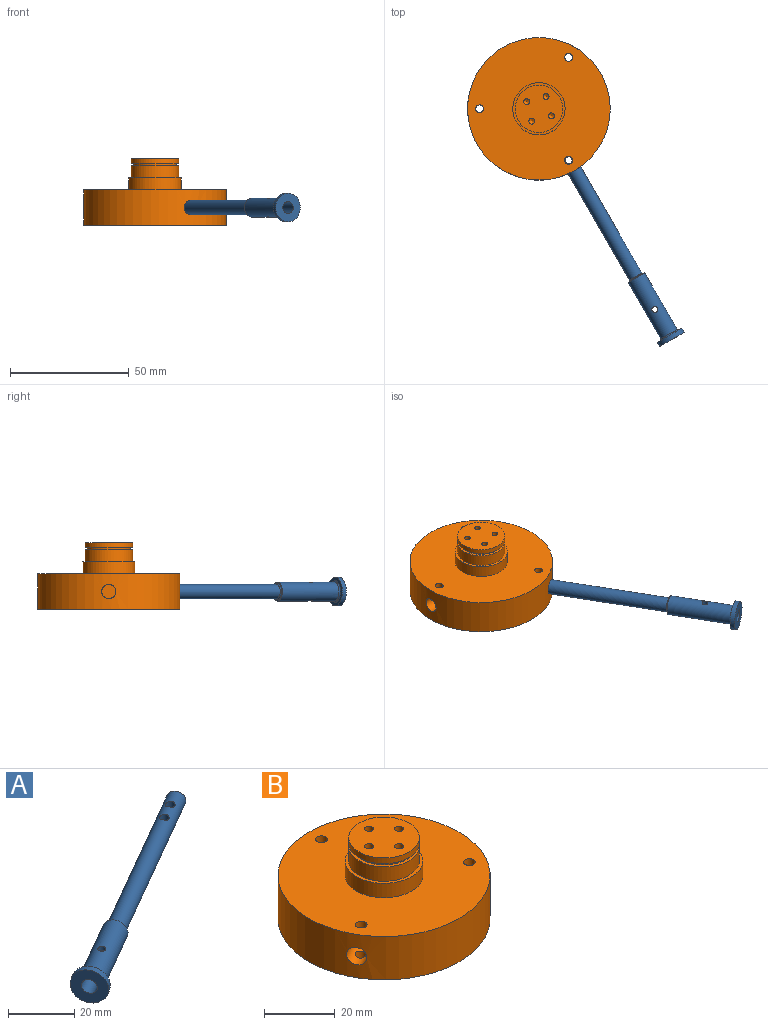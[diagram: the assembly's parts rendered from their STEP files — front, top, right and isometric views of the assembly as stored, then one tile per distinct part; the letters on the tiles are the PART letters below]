
ASSEMBLY  parts=2 mates=1
PART A: 16 faces, bbox 92.3x58.3x12 mm
  f0: cylinder r=6mm len=12mm, axis (0.87,0.5,0), area 75.4mm2, adj f1,f2
  f1: plane 12x10.39mm, normal (-0.87,-0.5,0), area 93.5mm2, adj f0,f10
  f2: plane 12x10.39mm, normal (0.87,0.5,0), area 49.5mm2, adj f0,f8
  f3: cylinder r=4mm len=27.82mm, axis (-0.87,-0.5,0), area 681.2mm2, adj f4,f8,f11,f12
  f4: plane 8x6.93mm, normal (0.87,0.5,0), area 11.8mm2, adj f3,f7
  f5: plane 4x3.46mm, normal (0.87,0.5,0), area 12.6mm2, adj f15
  f6: cylinder r=3mm len=64.05mm, axis (0.87,0.5,0), area 1299.6mm2, adj f7,f13,f14,f15
  f7: torus R=3.5mm, axis (0.87,0.5,0), area 15.7mm2, adj f4,f6
  f8: torus R=4.5mm, axis (-0.87,-0.5,0), area 20.6mm2, adj f2,f3
  f9: cone r=0mm half-angle=59deg, axis (-0.87,-0.5,0), area 22.9mm2, adj f10
  f10: cylinder r=2.5mm len=24.15mm, axis (-0.87,-0.5,0), area 382.5mm2, adj f1,f9,f11,f12
  f11: cylinder r=1.25mm len=2.5mm, axis (0,0,1), area 12.3mm2, adj f3,f10
  f12: cylinder r=1.25mm len=2.5mm, axis (0,0,1), area 12.3mm2, adj f3,f10
  f13: cylinder r=1.5mm len=6mm, axis (0,0,1), area 52.8mm2, adj f6
  f14: cylinder r=1.5mm len=6mm, axis (0,0,1), area 52.8mm2, adj f6
  f15: cone r=2mm half-angle=45deg, axis (-0.87,-0.5,0), area 22.2mm2, adj f5,f6
PART B: 33 faces, bbox 60x60x28.1 mm
  f0: cylinder r=3mm len=20.32mm, axis (0.87,0.5,0), area 357.7mm2, adj f3,f12,f13,f14
  f1: cylinder r=3mm len=20.32mm, axis (-0.87,0.5,0), area 357.7mm2, adj f3,f9,f10,f11
  f2: cylinder r=3mm len=20mm, axis (0,-1,0), area 357.7mm2, adj f3,f6,f7,f8
  f3: cylinder r=30mm len=60mm, axis (0,0,-1), area 2742.6mm2, adj f0,f1,f2,f4,f5
  f4: plane 60x60mm, normal (0,0,1), area 2421.6mm2, adj f3,f7,f10,f13,f15
  f5: plane 60x60mm, normal (0,0,-1), area 2793.2mm2, adj f3,f8,f11,f14,f24
  f6: plane 6x6mm, normal (0,1,0), area 28.3mm2, adj f2
  f7: cylinder r=1.65mm len=4.99mm, axis (0,0,1), area 49.2mm2, adj f2,f4
  f8: cylinder r=1.65mm len=4.99mm, axis (0,0,1), area 49.2mm2, adj f2,f5
  f9: plane 6x5.2mm, normal (0.87,-0.5,0), area 28.3mm2, adj f1
  f10: cylinder r=1.65mm len=4.99mm, axis (0,0,1), area 49.2mm2, adj f1,f4
  f11: cylinder r=1.65mm len=4.99mm, axis (0,0,1), area 49.2mm2, adj f1,f5
  f12: plane 6x5.2mm, normal (-0.87,-0.5,0), area 28.3mm2, adj f0
  f13: cylinder r=1.65mm len=4.99mm, axis (0,0,1), area 49.2mm2, adj f0,f4
  f14: cylinder r=1.65mm len=4.99mm, axis (0,0,1), area 49.2mm2, adj f0,f5
  f15: cylinder r=11mm len=22mm, axis (0,0,-1), area 345.6mm2, adj f4,f22
  f16: plane 20x20mm, normal (0,0,1), area 294.5mm2, adj f17,f26,f28,f30,f32
  f17: cylinder r=10mm len=20mm, axis (0,0,-1), area 125.7mm2, adj f16,f18
  f18: plane 20x20mm, normal (0,0,-1), area 59.7mm2, adj f17,f19
  f19: cylinder r=9mm len=18mm, axis (0,0,-1), area 62.2mm2, adj f18,f20
  f20: plane 20x20mm, normal (0,0,1), area 59.7mm2, adj f19,f21
  f21: cylinder r=10mm len=20mm, axis (0,0,-1), area 314.2mm2, adj f20,f22
  f22: plane 22x22mm, normal (0,0,1), area 66mm2, adj f15,f21
  f23: cone r=0mm half-angle=59deg, axis (0,0,-1), area 10mm2, adj f24
  f24: cylinder r=1.65mm len=15.01mm, axis (0,0,-1), area 155.6mm2, adj f5,f23
  f25: cone r=0mm half-angle=59deg, axis (0,0,1), area 5.7mm2, adj f26
  f26: cylinder r=1.25mm len=10mm, axis (0,0,1), area 78.5mm2, adj f16,f25
  f27: cone r=0mm half-angle=59deg, axis (0,0,1), area 5.7mm2, adj f28
  f28: cylinder r=1.25mm len=10mm, axis (0,0,1), area 78.5mm2, adj f16,f27
  f29: cone r=0mm half-angle=59deg, axis (0,0,1), area 5.7mm2, adj f30
  f30: cylinder r=1.25mm len=10mm, axis (0,0,1), area 78.5mm2, adj f16,f29
  f31: cone r=0mm half-angle=59deg, axis (0,0,1), area 5.7mm2, adj f32
  f32: cylinder r=1.25mm len=10mm, axis (0,0,1), area 78.5mm2, adj f16,f31
PLACE A rot(axis=(0,0,1),90deg) t=(-0.12,-0.79,-7.74)mm
PLACE B rot(axis=(0,0,-1),30deg) t=(-0.12,-0.79,-7.74)mm
MATE cylindrical B.f1 <-> A.f15  axis (-0.5,0.87,0) through (9.91,-18.17,-7.74)mm
